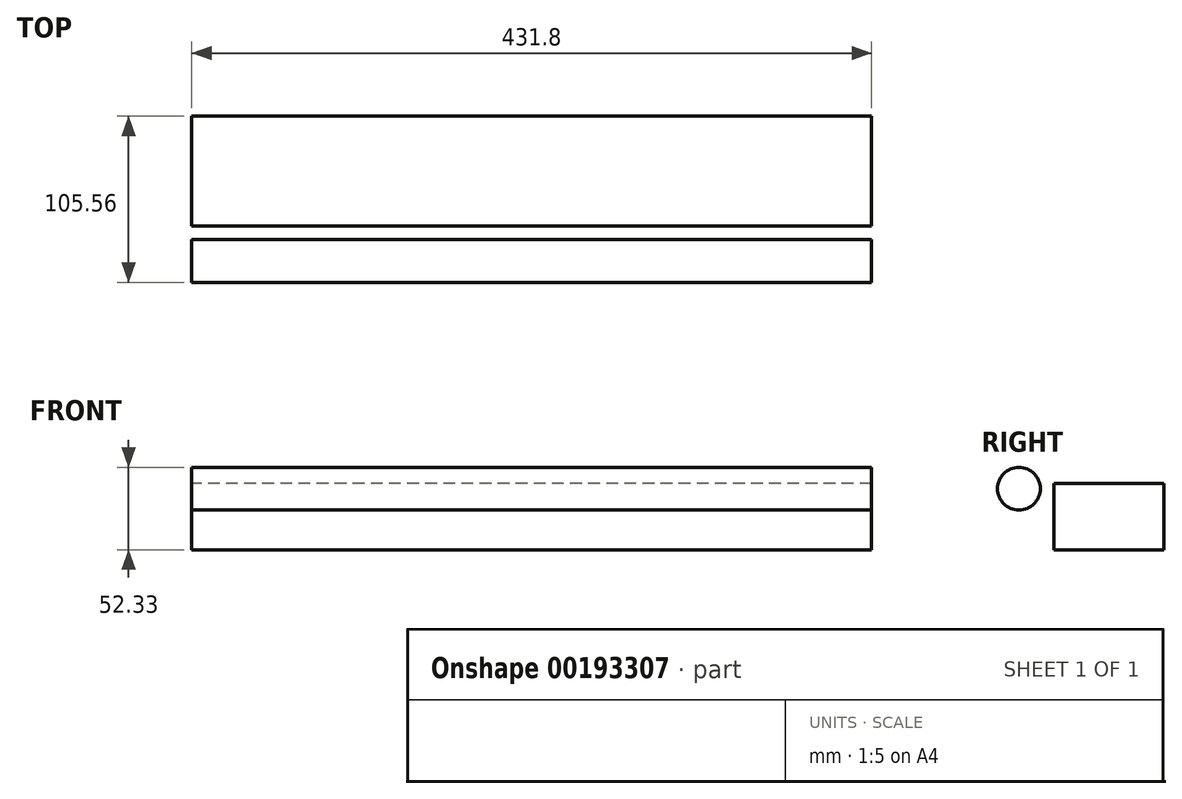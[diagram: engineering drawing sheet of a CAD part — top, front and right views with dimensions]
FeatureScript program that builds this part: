
annotation { "Feature Type Name" : "Feature", "Feature Type Description" : "" }
export const myFeature = defineFeature(function(context is Context, id is Id, definition is map)
    precondition{}
    {
        {
            var Q0;
            Q0=qCreatedBy(makeId("Right.planeOp"),FACE);
            var sketch = newSketch(context, id + "F0", { "sketchPlane" : qUnion([Q0])});
            skLineSegment(sketch, "E0.bottom", {"start": v(64.64, 58.03) * mm, "end": v(-5.25, 58.03) * mm});
            skLineSegment(sketch, "E0.top", {"start": v(64.64, 15.84) * mm, "end": v(-5.25, 15.84) * mm});
            skLineSegment(sketch, "E0.left", {"start": v(64.64, 58.03) * mm, "end": v(64.64, 15.84) * mm});
            skLineSegment(sketch, "E0.right", {"start": v(-5.25, 58.03) * mm, "end": v(-5.25, 15.84) * mm});
            skCircle(sketch, "E1", {"center": v(-27.34, 54.6) * mm, "radius": 13.58 * mm});
            skFitSpline(sketch, "E2", {"points": [v(-20.1, 18.2) * mm, v(-32.23, 29.42) * mm, v(-36.4, 13.85) * mm, v(-36.21, 14.03) * mm], "startDerivative": vector(-28.84, 44.4) * mm, "endDerivative": vector(3.56, 6.25) * mm});
            skFitSpline(sketch, "E3", {"points": [v(59.03, 43.55) * mm, v(40.2, 43.73) * mm], "startDerivative": vector(-18.83, 0.18) * mm, "endDerivative": vector(-18.83, 0.18) * mm});
            skSolve(sketch);
        }
        {
            var Q0;
            Q0 = qSketchRegion(id + "F0", true);
            extrude(context, id + "F1", {"entities" : qUnion([Q0]), "depth" : 431.8 * mm});
        }
    });
